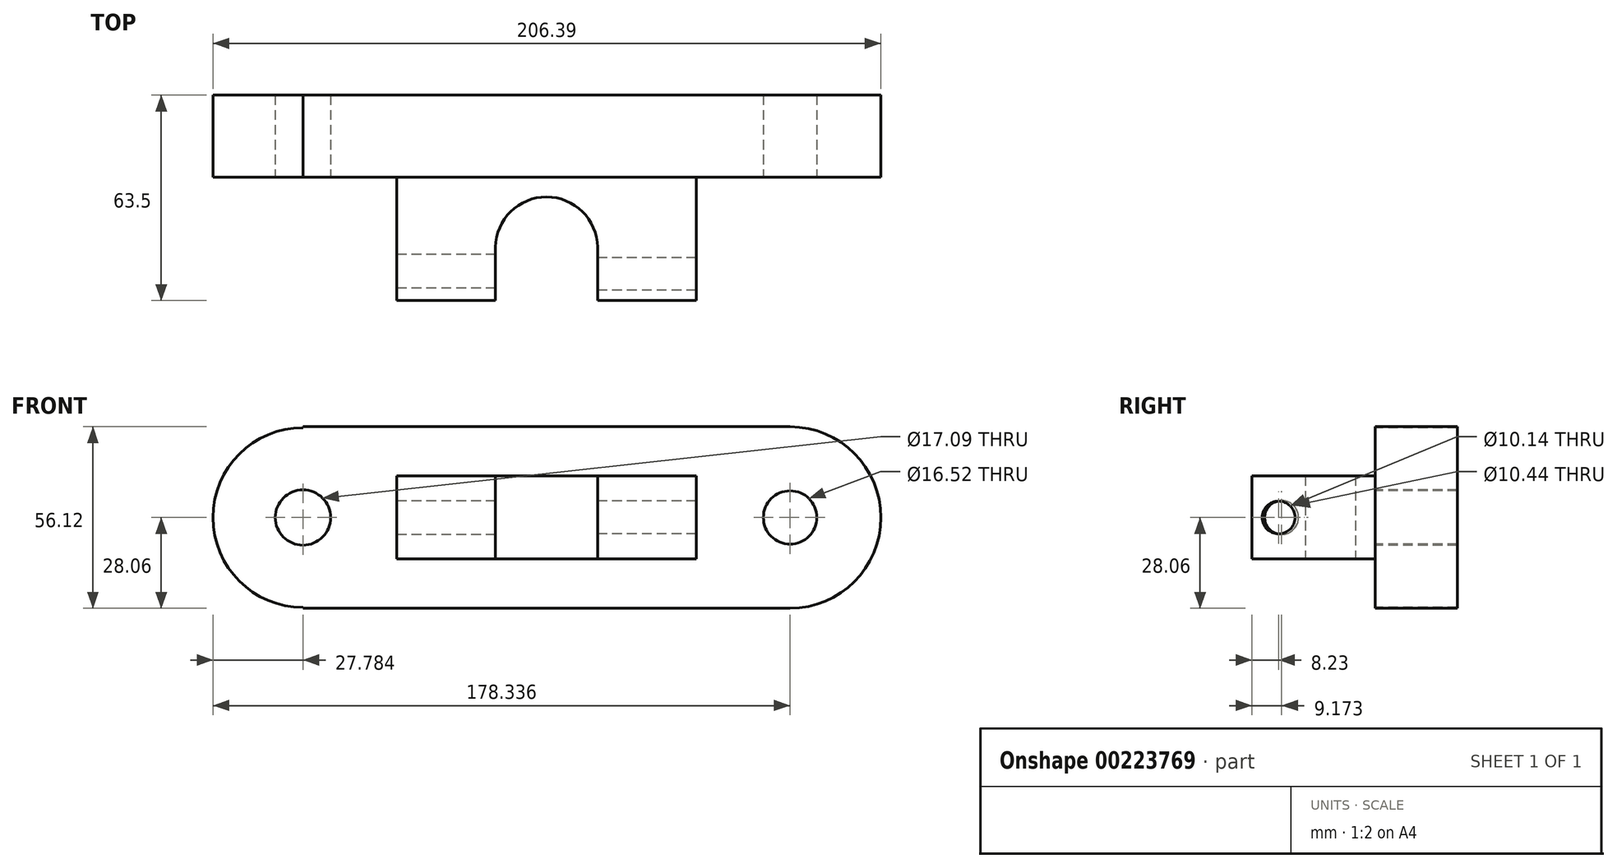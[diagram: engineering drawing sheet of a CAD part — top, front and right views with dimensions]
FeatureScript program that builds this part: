
annotation { "Feature Type Name" : "Feature", "Feature Type Description" : "" }
export const myFeature = defineFeature(function(context is Context, id is Id, definition is map)
    precondition{}
    {
        {
            var Q0;
            Q0=qCreatedBy(makeId("Front.planeOp"),FACE);
            var sketch = newSketch(context, id + "F0", { "sketchPlane" : qUnion([Q0])});
            skLineSegment(sketch, "E0.bottom", {"start": v(-75.28, 28.06) * mm, "end": v(75.28, 28.06) * mm});
            skLineSegment(sketch, "E0.top", {"start": v(-75.28, -28.06) * mm, "end": v(75.28, -28.06) * mm});
            skLineSegment(sketch, "E0.left", {"start": v(-75.28, 28.06) * mm, "end": v(-75.28, -28.06) * mm});
            skLineSegment(sketch, "E0.right", {"start": v(75.28, 28.06) * mm, "end": v(75.28, -28.06) * mm});
            skPoint(sketch, "E0.middle", {"position": v(0, 0) * mm});
            skSolve(sketch);
        }
        {
            var Q0;
            Q0=makeQuery(id+"F0.imprint","IMPRINT",FACE,{"disambiguationData":[TD([[makeQuery(id+"F0.imprint","IMPRINT",EDGE,{"derivedFrom":sQuery(id+"F0.wireOp",EDGE,"E0.bottom")}),-1.0]])]});
            var sketch = newSketch(context, id + "F1", { "sketchPlane" : qUnion([Q0])});
            skCircle(sketch, "E1", {"center": v(-75.15, 0) * mm, "radius": 28.04 * mm});
            skCircle(sketch, "E2", {"center": v(75.18, 0) * mm, "radius": 27.84 * mm});
            skSolve(sketch);
        }
        {
            var Q0;
            Q0=makeQuery(id+"F0.imprint","IMPRINT",FACE,{"disambiguationData":[TD([[makeQuery(id+"F0.imprint","IMPRINT",EDGE,{"derivedFrom":sQuery(id+"F0.wireOp",EDGE,"E0.bottom")}),-1.0]])]});
            var Q1;
            {var subQ0=sQuery(id+"F1.wireOp",EDGE,"E1");var subQ1=makeQuery(id+"F0.imprint","IMPRINT",EDGE,{"derivedFrom":sQuery(id+"F0.wireOp",EDGE,"E0.left")});var subQ2=makeQuery(id+"F1.imprint","INTERSECT",VERTEX,{"disambiguationData":[OD(0.0)],"derivedFrom":[subQ1,subQ0]});Q1=makeQuery(id+"F1.imprint","IMPRINT",FACE,{"disambiguationData":[TD([[makeQuery(id+"F1.imprint","IMPRINT",EDGE,{"disambiguationData":[TD([[subQ2,-1.0]])],"derivedFrom":subQ0}),1.0]])]});}
            var Q2;
            {var subQ0=sQuery(id+"F1.wireOp",EDGE,"E2");var subQ1=makeQuery(id+"F0.imprint","IMPRINT",EDGE,{"derivedFrom":sQuery(id+"F0.wireOp",EDGE,"E0.right")});var subQ2=makeQuery(id+"F1.imprint","INTERSECT",VERTEX,{"disambiguationData":[OD(0.0)],"derivedFrom":[subQ1,subQ0]});Q2=makeQuery(id+"F1.imprint","IMPRINT",FACE,{"disambiguationData":[TD([[makeQuery(id+"F1.imprint","IMPRINT",EDGE,{"disambiguationData":[TD([[subQ2,1.0]])],"derivedFrom":subQ0}),1.0]])]});}
            extrude(context, id + "F2", {"entities" : qUnion([Q0, Q1, Q2]), "depth" : 25.4 * mm});
        }
        {
            var Q0;
            Q0=makeQuery(id+"F2.opExtrude","SWEPT_BODY",BODY,{"disambiguationData":[OSD([sQuery(id+"F0.wireOp",EDGE,"E0.right"),sQuery(id+"F1.wireOp",EDGE,"E2")])]});
            deleteBodies(context, id + "F3", {"entities" : qUnion([Q0])});
        }
        {
            var Q0;
            Q0=makeQuery(id+"F2.opExtrude","SWEPT_BODY",BODY,{"disambiguationData":[OSD([sQuery(id+"F0.wireOp",EDGE,"E0.left"),sQuery(id+"F1.wireOp",EDGE,"E1")])]});
            deleteBodies(context, id + "F4", {"entities" : qUnion([Q0])});
        }
        {
            var Q0;
            Q0=makeQuery(id+"F2.opExtrude","CAP_FACE",FACE,{"disambiguationData":[OSD([sQuery(id+"F0.wireOp",EDGE,"E0.bottom"),sQuery(id+"F0.wireOp",EDGE,"E0.top"),sQuery(id+"F0.wireOp",EDGE,"E0.left"),sQuery(id+"F0.wireOp",EDGE,"E0.right")])],"isStart":false});
            var sketch = newSketch(context, id + "F5", { "sketchPlane" : qUnion([Q0])});
            skCircle(sketch, "E3", {"center": v(-75.28, 0) * mm, "radius": 27.79 * mm});
            skSolve(sketch);
        }
        {
            var Q0;
            {var subQ0=sQuery(id+"F5.wireOp",EDGE,"E3");var subQ1=sQuery(id+"F0.wireOp",EDGE,"E0.left");var subQ2=makeQuery(id+"F2.opExtrude","CAP_EDGE",EDGE,{"disambiguationData":[OSD([subQ1]),TDD([makeQuery(id+"F0.imprint","IMPRINT",EDGE,{"derivedFrom":subQ1})])],"isStart":false});var subQ3=makeQuery(id+"F5.imprint","INTERSECT",VERTEX,{"disambiguationData":[OD(0.0)],"derivedFrom":[subQ2,subQ0]});Q0=makeQuery(id+"F5.imprint","IMPRINT",FACE,{"disambiguationData":[TD([[makeQuery(id+"F5.imprint","IMPRINT",EDGE,{"disambiguationData":[TD([[subQ3,-1.0]])],"derivedFrom":subQ0}),1.0]])]});}
            extrude(context, id + "F6", {"entities" : qUnion([Q0]), "operationType" : NewBodyOperationType.ADD, "oppositeDirection" : true, "depth" : 25.4 * mm});
        }
        {
            var Q0;
            {var subQ0=sQuery(id+"F0.wireOp",EDGE,"E0.left");Q0=makeQuery(id+"F6.boolean.opBoolean","MERGE",FACE,{"derivedFrom":[makeQuery(id+"F2.opExtrude","CAP_FACE",FACE,{"disambiguationData":[OSD([sQuery(id+"F0.wireOp",EDGE,"E0.bottom"),sQuery(id+"F0.wireOp",EDGE,"E0.top"),subQ0,sQuery(id+"F0.wireOp",EDGE,"E0.right")])],"isStart":false}),makeQuery(id+"F6.opExtrude","CAP_FACE",FACE,{"disambiguationData":[OSD([subQ0,sQuery(id+"F5.wireOp",EDGE,"E3")])],"isStart":true})]});}
            var sketch = newSketch(context, id + "F7", { "sketchPlane" : qUnion([Q0])});
            skCircle(sketch, "E4", {"center": v(75.28, 0) * mm, "radius": 28.06 * mm});
            skSolve(sketch);
        }
        {
            var Q0;
            {var subQ1=sQuery(id+"F0.wireOp",EDGE,"E0.right");var subQ2=makeQuery(id+"F2.opExtrude","CAP_EDGE",EDGE,{"disambiguationData":[OSD([subQ1]),TDD([makeQuery(id+"F0.imprint","IMPRINT",EDGE,{"derivedFrom":subQ1})])],"isStart":false});Q0=makeQuery(id+"F7.imprint","IMPRINT",FACE,{"disambiguationData":[TD([[makeQuery(id+"F7.imprint","IMPRINT",EDGE,{"derivedFrom":subQ2}),1.0]])]});}
            extrude(context, id + "F8", {"entities" : qUnion([Q0]), "operationType" : NewBodyOperationType.ADD, "oppositeDirection" : true, "depth" : 25.4 * mm});
        }
        {
            var Q0;
            {var subQ0=sQuery(id+"F0.wireOp",EDGE,"E0.right");var subQ1=sQuery(id+"F0.wireOp",EDGE,"E0.left");Q0=makeQuery(id+"F8.boolean.opBoolean","MERGE",FACE,{"derivedFrom":[makeQuery(id+"F6.boolean.opBoolean","MERGE",FACE,{"derivedFrom":[makeQuery(id+"F2.opExtrude","CAP_FACE",FACE,{"disambiguationData":[OSD([sQuery(id+"F0.wireOp",EDGE,"E0.bottom"),sQuery(id+"F0.wireOp",EDGE,"E0.top"),subQ1,subQ0])],"isStart":false}),makeQuery(id+"F6.opExtrude","CAP_FACE",FACE,{"disambiguationData":[OSD([subQ1,sQuery(id+"F5.wireOp",EDGE,"E3")])],"isStart":true})]}),makeQuery(id+"F8.opExtrude","CAP_FACE",FACE,{"disambiguationData":[OSD([subQ0,sQuery(id+"F7.wireOp",EDGE,"E4")])],"isStart":true})]});}
            var sketch = newSketch(context, id + "F9", { "sketchPlane" : qUnion([Q0])});
            skCircle(sketch, "E5", {"center": v(-75.28, 0) * mm, "radius": 8.54 * mm});
            skCircle(sketch, "E6", {"center": v(75.28, 0) * mm, "radius": 8.56 * mm});
            skSolve(sketch);
        }
        {
            var Q0;
            Q0=makeQuery(id+"F9.imprint","IMPRINT",FACE,{"disambiguationData":[TD([[makeQuery(id+"F9.imprint","IMPRINT",EDGE,{"derivedFrom":sQuery(id+"F9.wireOp",EDGE,"E5")}),1.0]])]});
            extrude(context, id + "F10", {"entities" : qUnion([Q0]), "operationType" : NewBodyOperationType.REMOVE, "endBound" : BoundingType.THROUGH_ALL, "oppositeDirection" : true, "depth" : 25.4 * mm});
        }
        {
            var Q0;
            {var subQ0=sQuery(id+"F0.wireOp",EDGE,"E0.right");var subQ1=sQuery(id+"F0.wireOp",EDGE,"E0.left");Q0=makeQuery(id+"F8.boolean.opBoolean","MERGE",FACE,{"derivedFrom":[makeQuery(id+"F6.boolean.opBoolean","MERGE",FACE,{"derivedFrom":[makeQuery(id+"F2.opExtrude","CAP_FACE",FACE,{"disambiguationData":[OSD([sQuery(id+"F0.wireOp",EDGE,"E0.bottom"),sQuery(id+"F0.wireOp",EDGE,"E0.top"),subQ1,subQ0])],"isStart":false}),makeQuery(id+"F6.opExtrude","CAP_FACE",FACE,{"disambiguationData":[OSD([subQ1,sQuery(id+"F5.wireOp",EDGE,"E3")])],"isStart":true})]}),makeQuery(id+"F8.opExtrude","CAP_FACE",FACE,{"disambiguationData":[OSD([subQ0,sQuery(id+"F7.wireOp",EDGE,"E4")])],"isStart":true})]});}
            var sketch = newSketch(context, id + "F11", { "sketchPlane" : qUnion([Q0])});
            skCircle(sketch, "E7", {"center": v(75.28, 0) * mm, "radius": 8.26 * mm});
            skSolve(sketch);
        }
        {
            var Q0;
            Q0=makeQuery(id+"F11.imprint","IMPRINT",FACE,{"disambiguationData":[TD([[makeQuery(id+"F11.imprint","IMPRINT",EDGE,{"derivedFrom":sQuery(id+"F11.wireOp",EDGE,"E7")}),1.0]])]});
            extrude(context, id + "F12", {"entities" : qUnion([Q0]), "operationType" : NewBodyOperationType.REMOVE, "endBound" : BoundingType.THROUGH_ALL, "oppositeDirection" : true, "depth" : 25.4 * mm});
        }
        {
            var Q0;
            {var subQ0=sQuery(id+"F0.wireOp",EDGE,"E0.right");var subQ1=sQuery(id+"F0.wireOp",EDGE,"E0.left");Q0=makeQuery(id+"F8.boolean.opBoolean","MERGE",FACE,{"derivedFrom":[makeQuery(id+"F6.boolean.opBoolean","MERGE",FACE,{"derivedFrom":[makeQuery(id+"F2.opExtrude","CAP_FACE",FACE,{"disambiguationData":[OSD([sQuery(id+"F0.wireOp",EDGE,"E0.bottom"),sQuery(id+"F0.wireOp",EDGE,"E0.top"),subQ1,subQ0])],"isStart":false}),makeQuery(id+"F6.opExtrude","CAP_FACE",FACE,{"disambiguationData":[OSD([subQ1,sQuery(id+"F5.wireOp",EDGE,"E3")])],"isStart":true})]}),makeQuery(id+"F8.opExtrude","CAP_FACE",FACE,{"disambiguationData":[OSD([subQ0,sQuery(id+"F7.wireOp",EDGE,"E4")])],"isStart":true})]});}
            var sketch = newSketch(context, id + "F13", { "sketchPlane" : qUnion([Q0])});
            skLineSegment(sketch, "E8.bottom", {"start": v(-46.28, 12.82) * mm, "end": v(46.28, 12.82) * mm});
            skLineSegment(sketch, "E8.top", {"start": v(-46.28, -12.82) * mm, "end": v(46.28, -12.82) * mm});
            skLineSegment(sketch, "E8.left", {"start": v(-46.28, 12.82) * mm, "end": v(-46.28, -12.82) * mm});
            skLineSegment(sketch, "E8.right", {"start": v(46.28, 12.82) * mm, "end": v(46.28, -12.82) * mm});
            skPoint(sketch, "E8.middle", {"position": v(0, 0) * mm});
            skSolve(sketch);
        }
        {
            var Q0;
            Q0=makeQuery(id+"F13.imprint","IMPRINT",FACE,{"disambiguationData":[TD([[makeQuery(id+"F13.imprint","IMPRINT",EDGE,{"derivedFrom":sQuery(id+"F13.wireOp",EDGE,"E8.bottom")}),-1.0]])]});
            extrude(context, id + "F14", {"entities" : qUnion([Q0]), "operationType" : NewBodyOperationType.ADD, "depth" : 38.1 * mm});
        }
        {
            var Q0;
            Q0=makeQuery(id+"F14.opExtrude","SWEPT_FACE",FACE,{"disambiguationData":[OSD([sQuery(id+"F13.wireOp",EDGE,"E8.top")])]});
            var sketch = newSketch(context, id + "F15", { "sketchPlane" : qUnion([Q0])});
            skCircle(sketch, "E9", {"center": v(0, 47.22) * mm, "radius": 15.76 * mm});
            skSolve(sketch);
        }
        {
            var Q0;
            Q0=makeQuery(id+"F15.imprint","IMPRINT",FACE,{"disambiguationData":[TD([[makeQuery(id+"F15.imprint","IMPRINT",EDGE,{"derivedFrom":sQuery(id+"F15.wireOp",EDGE,"E9")}),1.0]])]});
            var sketch = newSketch(context, id + "F16", { "sketchPlane" : qUnion([Q0])});
            skLineSegment(sketch, "E10.bottom", {"start": v(15.84, 47) * mm, "end": v(-15.8, 47) * mm});
            skLineSegment(sketch, "E10.top", {"start": v(15.84, 68.7) * mm, "end": v(-15.8, 68.7) * mm});
            skLineSegment(sketch, "E10.left", {"start": v(15.84, 47) * mm, "end": v(15.84, 68.7) * mm});
            skLineSegment(sketch, "E10.right", {"start": v(-15.8, 47) * mm, "end": v(-15.8, 68.7) * mm});
            skSolve(sketch);
        }
        {
            var Q0;
            Q0=makeQuery(id+"F16.imprint","IMPRINT",FACE,{"disambiguationData":[TD([[makeQuery(id+"F16.imprint","IMPRINT",EDGE,{"derivedFrom":sQuery(id+"F16.wireOp",EDGE,"E10.top")}),1.0]])]});
            var Q1;
            {var subQ0=sQuery(id+"F16.wireOp",EDGE,"E10.bottom");var subQ1=makeQuery(id+"F15.imprint","IMPRINT",EDGE,{"derivedFrom":sQuery(id+"F15.wireOp",EDGE,"E9")});var subQ2=makeQuery(id+"F16.imprint","INTERSECT",VERTEX,{"disambiguationData":[OD(0.0)],"derivedFrom":[subQ1,subQ0]});Q1=makeQuery(id+"F16.imprint","IMPRINT",FACE,{"disambiguationData":[TD([[makeQuery(id+"F16.imprint","IMPRINT",EDGE,{"disambiguationData":[TD([[subQ2,-1.0]])],"derivedFrom":subQ0}),1.0]])]});}
            var Q2;
            Q2=makeQuery(id+"F15.imprint","IMPRINT",FACE,{"disambiguationData":[TD([[makeQuery(id+"F15.imprint","IMPRINT",EDGE,{"derivedFrom":sQuery(id+"F15.wireOp",EDGE,"E9")}),1.0]])]});
            extrude(context, id + "F17", {"entities" : qUnion([Q0, Q1, Q2]), "operationType" : NewBodyOperationType.REMOVE, "endBound" : BoundingType.THROUGH_ALL, "oppositeDirection" : true, "depth" : 25.4 * mm});
        }
        {
            var Q0;
            Q0=makeQuery(id+"F17.boolean.opBoolean","COPY",FACE,{"derivedFrom":makeQuery(id+"F17.opExtrude","SWEPT_FACE",FACE,{"disambiguationData":[OSD([sQuery(id+"F16.wireOp",EDGE,"E10.left")])]})});
            var sketch = newSketch(context, id + "F18", { "sketchPlane" : qUnion([Q0])});
            skCircle(sketch, "E11", {"center": v(55.27, 0) * mm, "radius": 5.07 * mm});
            skSolve(sketch);
        }
        {
            var Q0;
            Q0=makeQuery(id+"F18.imprint","IMPRINT",FACE,{"disambiguationData":[TD([[makeQuery(id+"F18.imprint","IMPRINT",EDGE,{"derivedFrom":sQuery(id+"F18.wireOp",EDGE,"E11")}),1.0]])]});
            extrude(context, id + "F19", {"entities" : qUnion([Q0]), "operationType" : NewBodyOperationType.REMOVE, "endBound" : BoundingType.THROUGH_ALL, "oppositeDirection" : true, "depth" : 25.4 * mm});
        }
        {
            var Q0;
            Q0=makeQuery(id+"F17.boolean.opBoolean","COPY",FACE,{"derivedFrom":makeQuery(id+"F17.opExtrude","SWEPT_FACE",FACE,{"disambiguationData":[OSD([sQuery(id+"F16.wireOp",EDGE,"E10.right")])]})});
            var sketch = newSketch(context, id + "F20", { "sketchPlane" : qUnion([Q0])});
            skCircle(sketch, "E12", {"center": v(-54.33, 0) * mm, "radius": 5.22 * mm});
            skSolve(sketch);
        }
        {
            var Q0;
            Q0=makeQuery(id+"F20.imprint","IMPRINT",FACE,{"disambiguationData":[TD([[makeQuery(id+"F20.imprint","IMPRINT",EDGE,{"derivedFrom":sQuery(id+"F20.wireOp",EDGE,"E12")}),1.0]])]});
            extrude(context, id + "F21", {"entities" : qUnion([Q0]), "operationType" : NewBodyOperationType.REMOVE, "endBound" : BoundingType.THROUGH_ALL, "oppositeDirection" : true, "depth" : 25.4 * mm});
        }
    });
